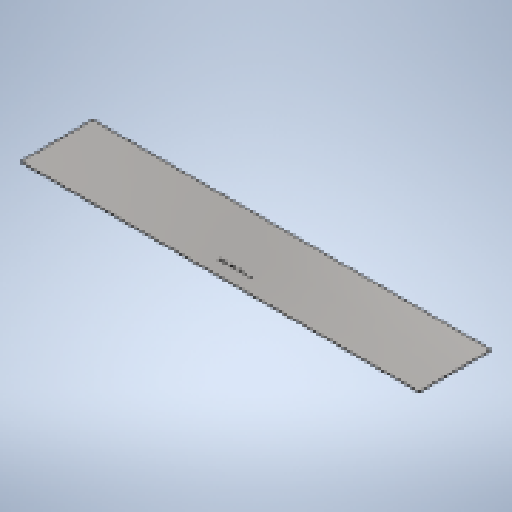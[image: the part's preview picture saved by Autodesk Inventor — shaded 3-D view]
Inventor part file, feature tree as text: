
AUTODESK INVENTOR PART (.ipt)
format: ipt  version: 2025 (Build 290162010, 162A)  size: 193,024 bytes
history: native  units: mm
features: other x2, sketch x2, sheet_metal_op x1
ambient origin geometry x8: Origin, YZ Plane, XZ Plane, XY Plane, X Axis, Y Axis, Z Axis, Center Point
bodies: Solid1 (feature_tree)
feature tree (5):
  sheet_metal_op  "Face1"
  other  "Mark1"
  sketch  "Sketch1"  dims[d0=1468.148307mm]
  other  "Plate1"
  sketch  "Sketch2"  dims[d1=267.044mm d2=2.0mm d3=12.0mm d4=110.0mm d5=50.0mm]
